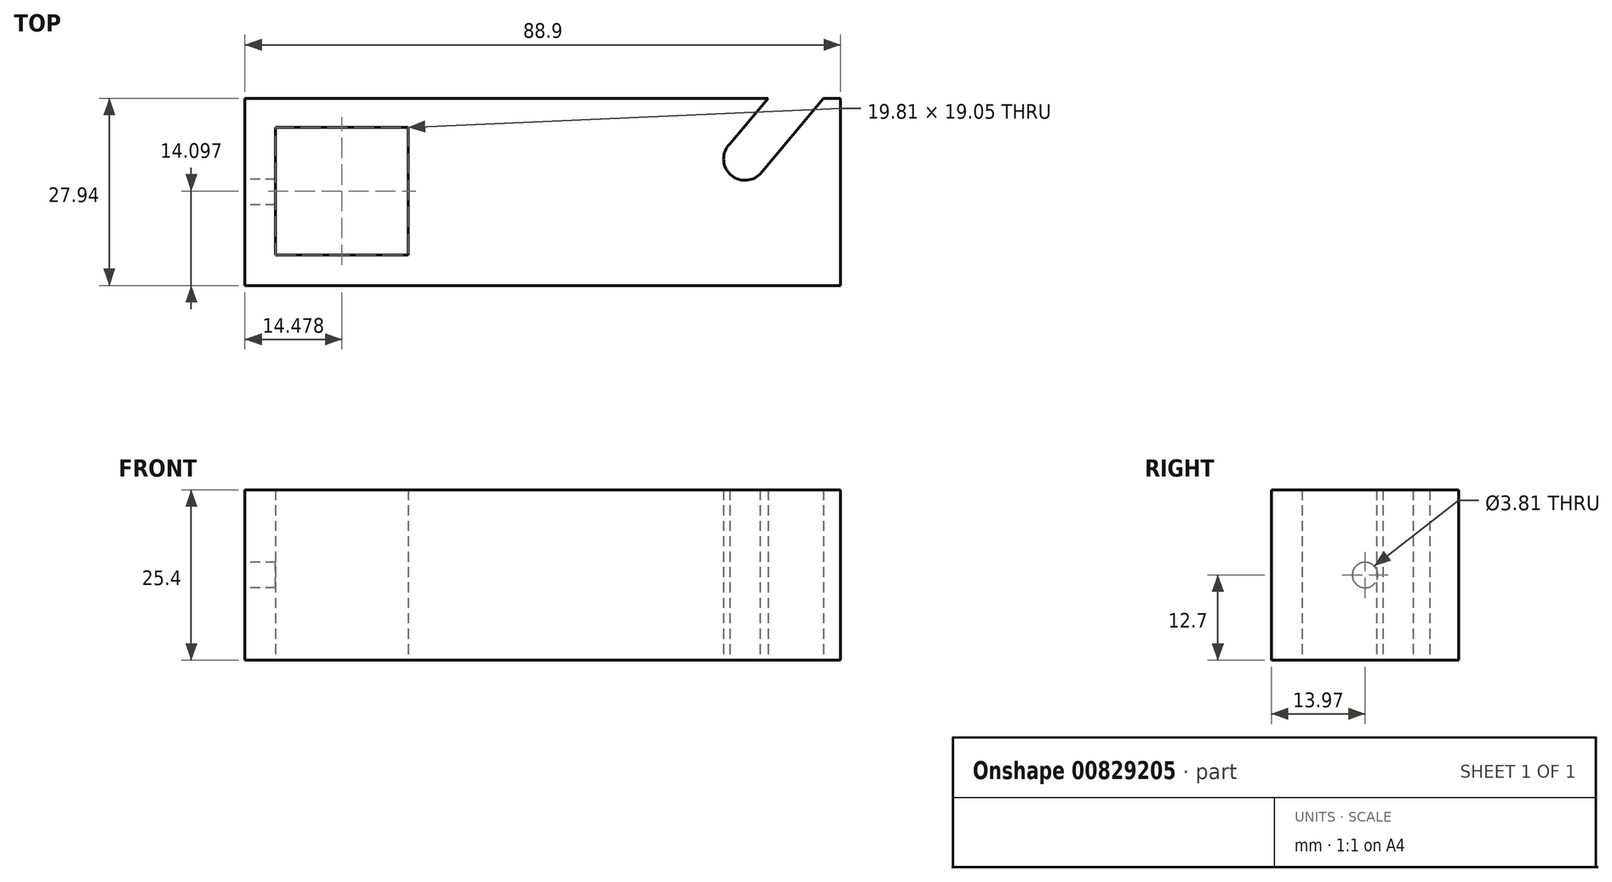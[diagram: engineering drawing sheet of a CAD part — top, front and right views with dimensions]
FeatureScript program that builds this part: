
annotation { "Feature Type Name" : "Feature", "Feature Type Description" : "" }
export const myFeature = defineFeature(function(context is Context, id is Id, definition is map)
    precondition{}
    {
        {
            var Q0;
            Q0=qCreatedBy(makeId("Top.planeOp"),FACE);
            var sketch = newSketch(context, id + "F0", { "sketchPlane" : qUnion([Q0])});
            skLineSegment(sketch, "E0.bottom", {"start": v(0, 0) * mm, "end": v(78.07, 0) * mm});
            skLineSegment(sketch, "E0.top", {"start": v(0, -27.94) * mm, "end": v(88.9, -27.94) * mm});
            skLineSegment(sketch, "E0.left", {"start": v(0, 0) * mm, "end": v(0, -27.94) * mm});
            skLineSegment(sketch, "E0.right", {"start": v(88.9, 0) * mm, "end": v(88.9, -27.94) * mm});
            skLineSegment(sketch, "E1", {"start": v(86.36, 0) * mm, "end": v(76.88, -11.3) * mm});
            skLineSegment(sketch, "E2", {"start": v(72.36, -6.81) * mm, "end": v(78.07, 0) * mm});
            skArc(sketch, "E3", {"start": v(72.36, -6.81) * mm, "mid": v(72.38, -11.32) * mm, "end": v(76.88, -11.3) * mm});
            skLineSegment(sketch, "E4.trimOffspring", {"start": v(86.36, 0) * mm, "end": v(88.9, 0) * mm});
            skLineSegment(sketch, "E5.bottom", {"start": v(4.57, -4.32) * mm, "end": v(24.38, -4.32) * mm});
            skLineSegment(sketch, "E5.top", {"start": v(4.57, -23.37) * mm, "end": v(24.38, -23.37) * mm});
            skLineSegment(sketch, "E5.left", {"start": v(4.57, -4.32) * mm, "end": v(4.57, -23.37) * mm});
            skLineSegment(sketch, "E5.right", {"start": v(24.38, -4.32) * mm, "end": v(24.38, -23.37) * mm});
            skSolve(sketch);
        }
        {
            var Q0;
            Q0=makeQuery(id+"F0.imprint","IMPRINT",FACE,{"disambiguationData":[TD([[makeQuery(id+"F0.imprint","IMPRINT",EDGE,{"derivedFrom":sQuery(id+"F0.wireOp",EDGE,"E0.bottom")}),-1.0]])]});
            extrude(context, id + "F1", {"entities" : qUnion([Q0]), "depth" : 25.4 * mm, "offsetDistance" : 25.4 * mm});
        }
        {
            var Q0;
            Q0=makeQuery(id+"F1.opExtrude","SWEPT_FACE",FACE,{"disambiguationData":[OSD([sQuery(id+"F0.wireOp",EDGE,"E0.left")])]});
            var sketch = newSketch(context, id + "F2", { "sketchPlane" : qUnion([Q0])});
            skCircle(sketch, "E6", {"center": v(13.97, 12.7) * mm, "radius": 1.9 * mm});
            skSolve(sketch);
        }
        {
            var Q0;
            Q0=makeQuery(id+"F2.imprint","IMPRINT",FACE,{"disambiguationData":[TD([[makeQuery(id+"F2.imprint","IMPRINT",EDGE,{"derivedFrom":sQuery(id+"F2.wireOp",EDGE,"E6")}),1.0]])]});
            extrude(context, id + "F3", {"entities" : qUnion([Q0]), "operationType" : NewBodyOperationType.REMOVE, "oppositeDirection" : true, "depth" : 7.62 * mm, "offsetDistance" : 25.4 * mm});
        }
    });
